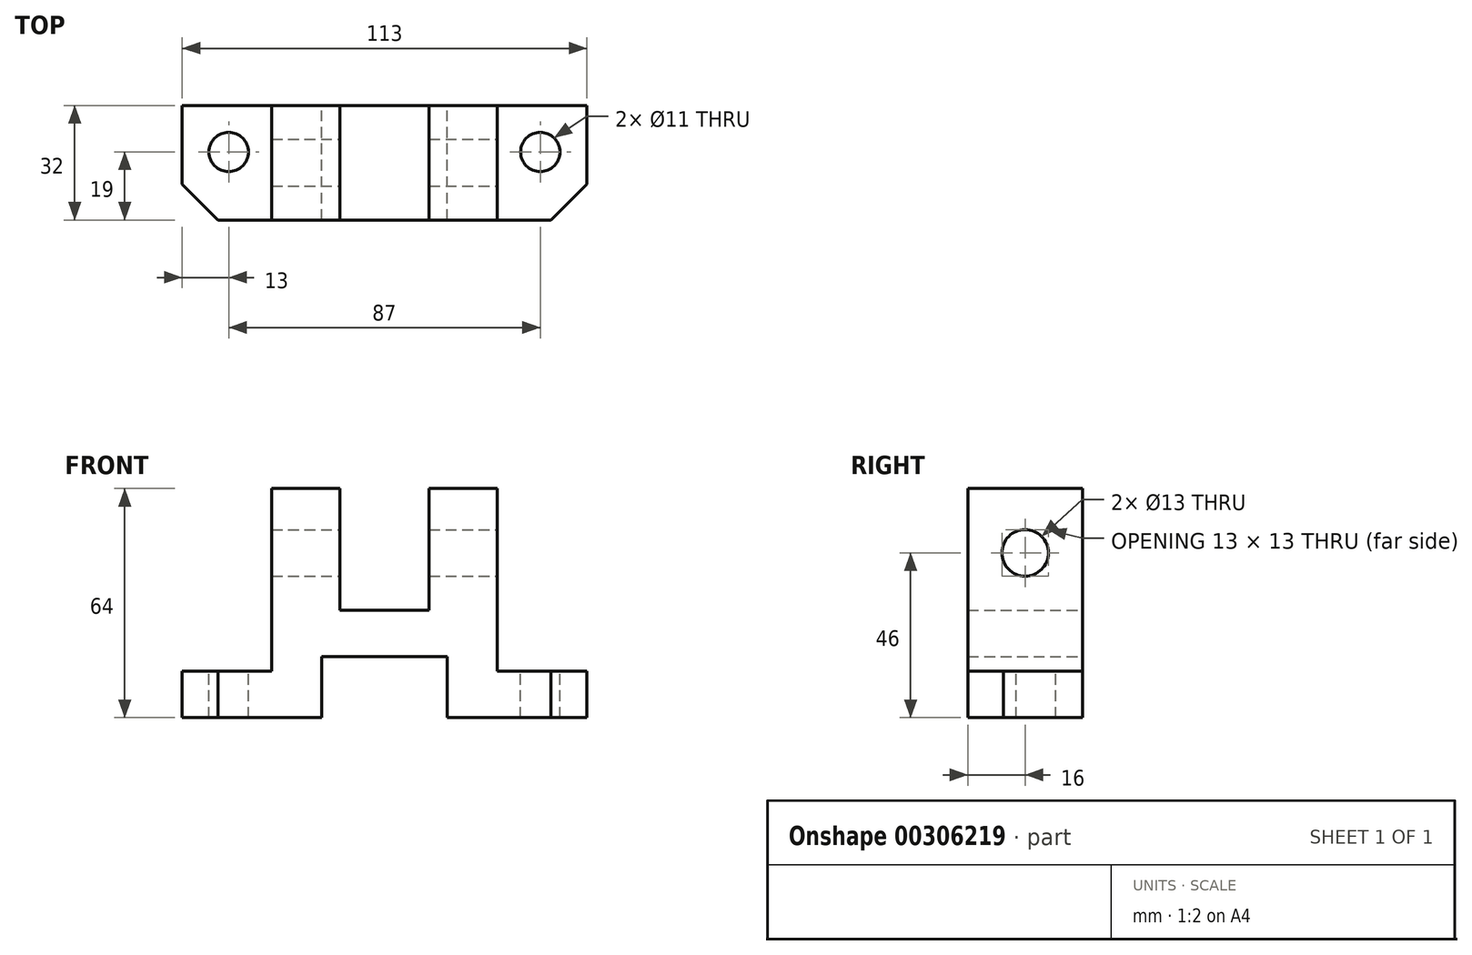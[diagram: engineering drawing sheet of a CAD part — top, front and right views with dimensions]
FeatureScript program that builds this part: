
annotation { "Feature Type Name" : "Feature", "Feature Type Description" : "" }
export const myFeature = defineFeature(function(context is Context, id is Id, definition is map)
    precondition{}
    {
        {
            var Q0;
            Q0=qCreatedBy(makeId("Front.planeOp"),FACE);
            var sketch = newSketch(context, id + "F0", { "sketchPlane" : qUnion([Q0])});
            skLineSegment(sketch, "E0", {"start": v(0, 0) * mm, "end": v(0, 13) * mm});
            skLineSegment(sketch, "E1", {"start": v(0, 13) * mm, "end": v(25, 13) * mm});
            skLineSegment(sketch, "E2", {"start": v(25, 13) * mm, "end": v(25, 64) * mm});
            skLineSegment(sketch, "E3", {"start": v(25, 64) * mm, "end": v(44, 64) * mm});
            skLineSegment(sketch, "E4", {"start": v(44, 64) * mm, "end": v(44, 30) * mm});
            skLineSegment(sketch, "E5", {"start": v(44, 30) * mm, "end": v(69, 30) * mm});
            skLineSegment(sketch, "E6", {"start": v(69, 30) * mm, "end": v(69, 64) * mm});
            skLineSegment(sketch, "E7", {"start": v(69, 64) * mm, "end": v(88, 64) * mm});
            skLineSegment(sketch, "E8", {"start": v(88, 64) * mm, "end": v(88, 13) * mm});
            skLineSegment(sketch, "E9", {"start": v(88, 13) * mm, "end": v(113, 13) * mm});
            skLineSegment(sketch, "E10", {"start": v(113, 13) * mm, "end": v(113, 0) * mm});
            skLineSegment(sketch, "E11", {"start": v(113, 0) * mm, "end": v(74, 0) * mm});
            skLineSegment(sketch, "E12", {"start": v(74, 0) * mm, "end": v(74, 17) * mm});
            skLineSegment(sketch, "E13", {"start": v(74, 17) * mm, "end": v(39, 17) * mm});
            skLineSegment(sketch, "E14", {"start": v(39, 17) * mm, "end": v(39, 0) * mm});
            skLineSegment(sketch, "E15", {"start": v(39, 0) * mm, "end": v(0, 0) * mm});
            skSolve(sketch);
        }
        {
            var Q0;
            Q0 = qSketchRegion(id + "F0", true);
            extrude(context, id + "F1", {"entities" : qUnion([Q0]), "depth" : 32 * mm});
        }
        {
            var Q0;
            Q0=makeQuery(id+"F1.opExtrude","SWEPT_FACE",FACE,{"disambiguationData":[OSD([sQuery(id+"F0.wireOp",EDGE,"E8")])]});
            var sketch = newSketch(context, id + "F2", { "sketchPlane" : qUnion([Q0])});
            skCircle(sketch, "E16", {"center": v(-16, 46) * mm, "radius": 6.5 * mm});
            skArc(sketch, "E17", {"start": v(-32, 60.14) * mm, "mid": v(-16, 64) * mm, "end": v(0, 60.12) * mm});
            skSolve(sketch);
        }
        {
            var Q0;
            Q0=makeQuery(id+"F2.imprint","IMPRINT",FACE,{"disambiguationData":[TD([[makeQuery(id+"F2.imprint","IMPRINT",EDGE,{"derivedFrom":sQuery(id+"F2.wireOp",EDGE,"E16")}),1.0]])]});
            var Q1;
            {var subQ0=sQuery(id+"F2.wireOp",EDGE,"E17");var subQ1=sQuery(id+"F0.wireOp",EDGE,"E8");var subQ2=makeQuery(id+"F1.opExtrude","CAP_EDGE",EDGE,{"disambiguationData":[OSD([subQ1])],"isStart":true});var subQ3=makeQuery(id+"F2.imprint","INTERSECT",VERTEX,{"derivedFrom":[subQ2,subQ0]});Q1=makeQuery(id+"F2.imprint","IMPRINT",FACE,{"disambiguationData":[TD([[makeQuery(id+"F2.imprint","IMPRINT",EDGE,{"disambiguationData":[TD([[subQ3,1.0]])],"derivedFrom":subQ0}),1.0]])]});}
            var Q2;
            {var subQ0=sQuery(id+"F2.wireOp",EDGE,"E17");var subQ1=sQuery(id+"F0.wireOp",EDGE,"E8");var subQ2=makeQuery(id+"F1.opExtrude","CAP_EDGE",EDGE,{"disambiguationData":[OSD([subQ1])],"isStart":false});var subQ3=makeQuery(id+"F2.imprint","INTERSECT",VERTEX,{"derivedFrom":[subQ2,subQ0]});Q2=makeQuery(id+"F2.imprint","IMPRINT",FACE,{"disambiguationData":[TD([[makeQuery(id+"F2.imprint","IMPRINT",EDGE,{"disambiguationData":[TD([[subQ3,-1.0]])],"derivedFrom":subQ0}),1.0]])]});}
            extrude(context, id + "F3", {"entities" : qUnion([Q0, Q1, Q2]), "operationType" : NewBodyOperationType.REMOVE, "endBound" : BoundingType.THROUGH_ALL, "oppositeDirection" : true, "depth" : 25 * mm});
        }
        {
            var Q0;
            Q0=makeQuery(id+"F1.opExtrude","SWEPT_FACE",FACE,{"disambiguationData":[OSD([sQuery(id+"F0.wireOp",EDGE,"E9")])]});
            var sketch = newSketch(context, id + "F4", { "sketchPlane" : qUnion([Q0])});
            skLineSegment(sketch, "E18", {"start": v(103, -32) * mm, "end": v(113, -22) * mm});
            skCircle(sketch, "E19", {"center": v(100, -13) * mm, "radius": 5.5 * mm});
            skSolve(sketch);
        }
        {
            var Q0;
            Q0=makeQuery(id+"F4.imprint","IMPRINT",FACE,{"disambiguationData":[TD([[makeQuery(id+"F4.imprint","IMPRINT",EDGE,{"derivedFrom":sQuery(id+"F4.wireOp",EDGE,"E19")}),1.0]])]});
            var Q1;
            {var subQ0=sQuery(id+"F4.wireOp",EDGE,"E18");Q1=makeQuery(id+"F4.imprint","IMPRINT",FACE,{"disambiguationData":[TD([[makeQuery(id+"F4.imprint","IMPRINT",EDGE,{"derivedFrom":subQ0}),-1.0]])]});}
            extrude(context, id + "F5", {"entities" : qUnion([Q0, Q1]), "operationType" : NewBodyOperationType.REMOVE, "endBound" : BoundingType.THROUGH_ALL, "oppositeDirection" : true, "depth" : 25 * mm});
        }
        {
            var Q0;
            Q0=makeQuery(id+"F1.opExtrude","SWEPT_FACE",FACE,{"disambiguationData":[OSD([sQuery(id+"F0.wireOp",EDGE,"E1")])]});
            var sketch = newSketch(context, id + "F6", { "sketchPlane" : qUnion([Q0])});
            skLineSegment(sketch, "E20", {"start": v(10, -32) * mm, "end": v(0, -22) * mm});
            skCircle(sketch, "E21", {"center": v(13, -13) * mm, "radius": 5.5 * mm});
            skSolve(sketch);
        }
        {
            var Q0;
            Q0=makeQuery(id+"F6.imprint","IMPRINT",FACE,{"disambiguationData":[TD([[makeQuery(id+"F6.imprint","IMPRINT",EDGE,{"derivedFrom":sQuery(id+"F6.wireOp",EDGE,"E21")}),1.0]])]});
            var Q1;
            {var subQ0=sQuery(id+"F6.wireOp",EDGE,"E20");Q1=makeQuery(id+"F6.imprint","IMPRINT",FACE,{"disambiguationData":[TD([[makeQuery(id+"F6.imprint","IMPRINT",EDGE,{"derivedFrom":subQ0}),1.0]])]});}
            extrude(context, id + "F7", {"entities" : qUnion([Q0, Q1]), "operationType" : NewBodyOperationType.REMOVE, "endBound" : BoundingType.THROUGH_ALL, "oppositeDirection" : true, "depth" : 25 * mm});
        }
    });
